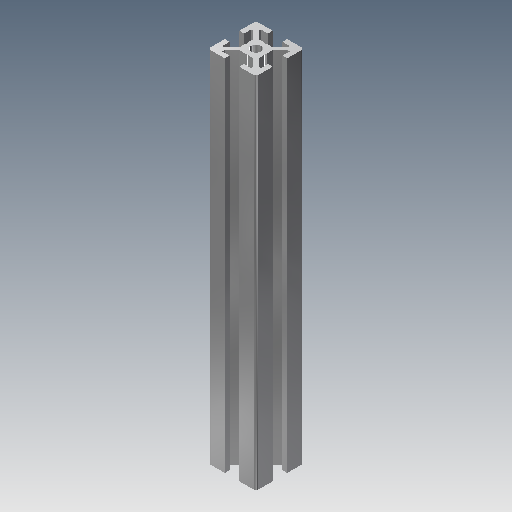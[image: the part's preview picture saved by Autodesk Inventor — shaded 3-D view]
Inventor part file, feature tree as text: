
AUTODESK INVENTOR PART (.ipt)
format: ipt  version: 2018.2 (Build 222227000, 227)  size: 167,936 bytes
history: native  units: mm
features: extrude x1, sketch x1
ambient origin geometry x8: Origin, YZ Plane, XZ Plane, XY Plane, X Axis, Y Axis, Z Axis, Center Point
bodies: Solid1 (feature_tree)
feature tree (2):
  extrude  "Extrusion1"  [1 undecoded]
  sketch  "Sketch1"  dims[d0=150.0mm d1=0.0mm]
note: 1 required parameter value undecoded (feature->parameter linkage not recoverable at this tier; creation-order binding heuristic only, values carry confidence <= 0.55)
